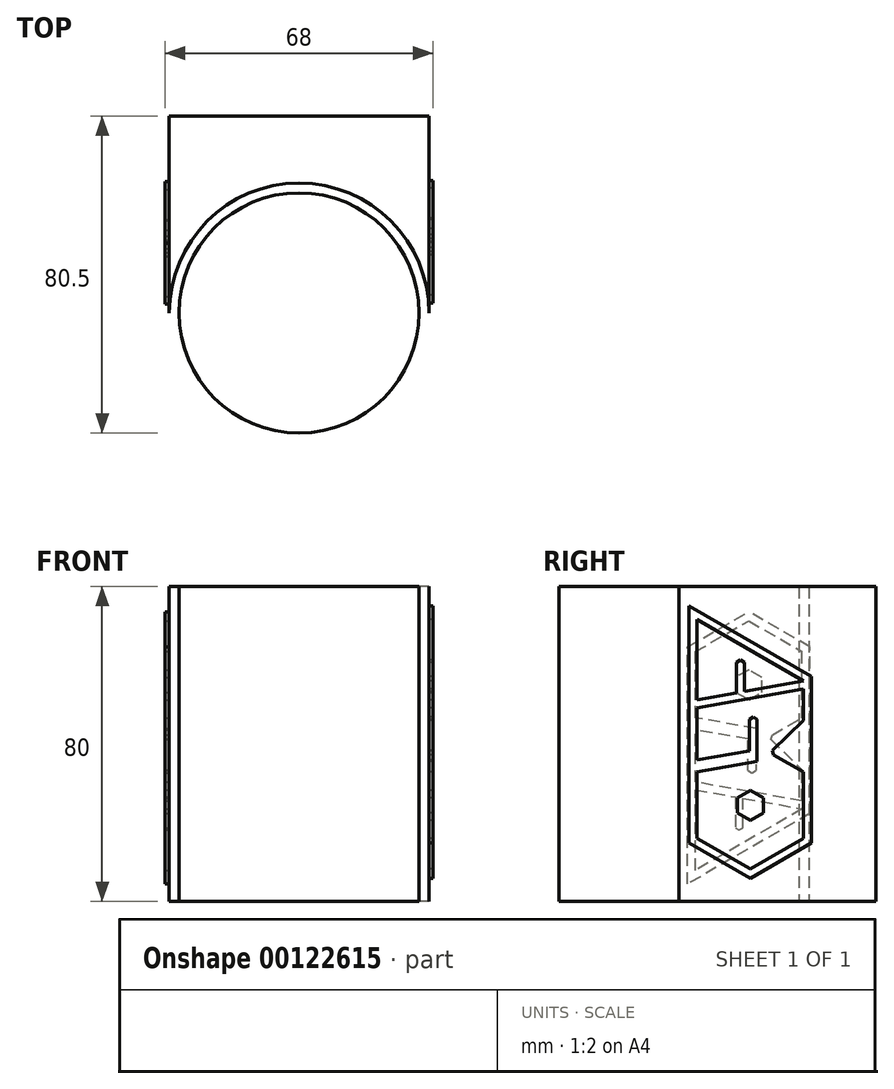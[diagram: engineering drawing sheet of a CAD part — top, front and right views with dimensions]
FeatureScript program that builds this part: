
annotation { "Feature Type Name" : "Feature", "Feature Type Description" : "" }
export const myFeature = defineFeature(function(context is Context, id is Id, definition is map)
    precondition{}
    {
        {
            var Q0;
            Q0=qCreatedBy(makeId("Top.planeOp"),FACE);
            var sketch = newSketch(context, id + "F5", { "sketchPlane" : qUnion([Q0])});
            skLineSegment(sketch, "E0", {"start": v(-33, 0) * mm, "end": v(-33, 50) * mm});
            skLineSegment(sketch, "E1.MirrorCS", {"start": v(-33, 50) * mm, "end": v(-79, 50) * mm});
            skLineSegment(sketch, "E2.MirrorCS", {"start": v(-79, 35) * mm, "end": v(-79, 50) * mm});
            skLineSegment(sketch, "E3.MirrorCS", {"start": v(-79, 35) * mm, "end": v(-99, 35) * mm});
            skLineSegment(sketch, "E4.MirrorCS", {"start": v(-99, 35) * mm, "end": v(-99, 0) * mm});
            skCircle(sketch, "E5.MirrorC", {"center": v(-66, 0) * mm, "radius": 33 * mm});
            skCircle(sketch, "E6.MirrorC", {"center": v(-66, 0) * mm, "radius": 30.5 * mm});
            skLineSegment(sketch, "E7", {"start": v(-99, 35) * mm, "end": v(-99, 50) * mm});
            skLineSegment(sketch, "E8", {"start": v(-99, 50) * mm, "end": v(-79, 50) * mm});
            skSolve(sketch);
        }
        {
            var Q0;
            {var subQ0=sQuery(id+"F5.wireOp",EDGE,"E0");Q0=makeQuery(id+"F5.imprint","IMPRINT",FACE,{"disambiguationData":[TD([[makeQuery(id+"F5.imprint","IMPRINT",EDGE,{"derivedFrom":subQ0}),1.0]])]});}
            var Q1;
            Q1=makeQuery(id+"F5.imprint","IMPRINT",FACE,{"disambiguationData":[TD([[makeQuery(id+"F5.imprint","IMPRINT",EDGE,{"derivedFrom":sQuery(id+"F5.wireOp",EDGE,"E6.MirrorC")}),1.0]])]});
            var Q2;
            Q2=makeQuery(id+"F5.imprint","IMPRINT",FACE,{"disambiguationData":[TD([[makeQuery(id+"F5.imprint","IMPRINT",EDGE,{"derivedFrom":sQuery(id+"F5.wireOp",EDGE,"E2.MirrorCS")}),1.0]])]});
            extrude(context, id + "F0", {"entities" : qUnion([Q0, Q1, Q2]), "depth" : 80 * mm});
        }
        {
            var Q0;
            Q0=makeQuery(id+"F0.opExtrude","SWEPT_FACE",FACE,{"disambiguationData":[OSD([sQuery(id+"F5.wireOp",EDGE,"E0")])]});
            var sketch = newSketch(context, id + "F1", { "sketchPlane" : qUnion([Q0])});
            skLineSegment(sketch, "E9", {"start": v(4.56, 71.6) * mm, "end": v(4.56, 51.17) * mm});
            skLineSegment(sketch, "E10", {"start": v(4.56, 51.17) * mm, "end": v(31.66, 55.94) * mm});
            skLineSegment(sketch, "E11", {"start": v(31.66, 55.94) * mm, "end": v(4.56, 71.6) * mm});
            skLineSegment(sketch, "E12", {"start": v(14.65, 52.94) * mm, "end": v(14.65, 60.74) * mm});
            skLineSegment(sketch, "E13", {"start": v(4.56, 51.17) * mm, "end": v(4.56, 16.02) * mm});
            skLineSegment(sketch, "E14", {"start": v(31.66, 55.94) * mm, "end": v(31.66, 16.02) * mm});
            skLineSegment(sketch, "E15", {"start": v(4.56, 16.02) * mm, "end": v(18.11, 8.2) * mm});
            skLineSegment(sketch, "E16", {"start": v(18.11, 8.2) * mm, "end": v(31.66, 16.02) * mm});
            skPoint(sketch, "E17.endSnap0", {"position": v(18.11, 53.55) * mm});
            skLineSegment(sketch, "E18.0", {"start": v(33.66, 57.1) * mm, "end": v(33.66, 15.6) * mm});
            skLineSegment(sketch, "E18.1", {"start": v(2.56, 75.05) * mm, "end": v(2.56, 51.65) * mm});
            skLineSegment(sketch, "E18.2", {"start": v(2.56, 51.65) * mm, "end": v(2.56, 14.87) * mm});
            skLineSegment(sketch, "E18.3", {"start": v(33.66, 57.1) * mm, "end": v(2.56, 75.05) * mm});
            skLineSegment(sketch, "E18.4", {"start": v(2.56, 14.87) * mm, "end": v(18.11, 5.89) * mm});
            skLineSegment(sketch, "E19", {"start": v(16.65, 60.74) * mm, "end": v(16.65, 53.3) * mm});
            skLineSegment(sketch, "E20", {"start": v(31.66, 53.94) * mm, "end": v(4.56, 49.17) * mm});
            skLineSegment(sketch, "E21", {"start": v(31.66, 55.94) * mm, "end": v(31.66, 53.94) * mm});
            skLineSegment(sketch, "E22", {"start": v(4.56, 36.26) * mm, "end": v(4.56, 38.26) * mm});
            skLineSegment(sketch, "E23", {"start": v(17.87, 46.23) * mm, "end": v(17.87, 38.26) * mm});
            skLineSegment(sketch, "E24", {"start": v(19.87, 35.53) * mm, "end": v(19.87, 46.23) * mm});
            skLineSegment(sketch, "E25", {"start": v(23.78, 38.34) * mm, "end": v(31.66, 46.02) * mm});
            skLineSegment(sketch, "E26", {"start": v(14.65, 60.74) * mm, "end": v(15.65, 61.32) * mm});
            skLineSegment(sketch, "E27", {"start": v(15.65, 61.32) * mm, "end": v(16.65, 60.74) * mm});
            skLineSegment(sketch, "E28", {"start": v(17.87, 46.23) * mm, "end": v(18.87, 46.8) * mm});
            skLineSegment(sketch, "E29", {"start": v(18.87, 46.8) * mm, "end": v(19.87, 46.23) * mm});
            skLineSegment(sketch, "E30", {"start": v(25.18, 36.9) * mm, "end": v(31.66, 43.27) * mm});
            skLineSegment(sketch, "E31", {"start": v(23.78, 38.34) * mm, "end": v(24.07, 37.21) * mm});
            skLineSegment(sketch, "E32", {"start": v(24.07, 37.21) * mm, "end": v(25.18, 36.9) * mm});
            skLineSegment(sketch, "E33", {"start": v(17.87, 38.26) * mm, "end": v(4.56, 35.91) * mm});
            skLineSegment(sketch, "E34", {"start": v(19.87, 35.53) * mm, "end": v(4.56, 32.83) * mm});
            skLineSegment(sketch, "E35", {"start": v(24.07, 37.21) * mm, "end": v(31.66, 32.83) * mm});
            skLineSegment(sketch, "E36", {"start": v(31.66, 32.83) * mm, "end": v(31.66, 16.02) * mm});
            skLineSegment(sketch, "E37", {"start": v(4.56, 32.83) * mm, "end": v(4.56, 16.02) * mm});
            skPoint(sketch, "E38", {"position": v(31.66, 24.42) * mm});
            skPoint(sketch, "E39", {"position": v(18.11, 24.42) * mm});
            skCircle(sketch, "E40.cCircle", {"center": v(18.11, 24.42) * mm, "radius": 3.3 * mm, "construction": true});
            skLineSegment(sketch, "E40.0", {"start": v(21.41, 26.33) * mm, "end": v(21.41, 22.52) * mm});
            skLineSegment(sketch, "E40.1", {"start": v(21.41, 22.52) * mm, "end": v(18.11, 20.61) * mm});
            skLineSegment(sketch, "E40.2", {"start": v(18.11, 20.61) * mm, "end": v(14.81, 22.52) * mm});
            skLineSegment(sketch, "E40.3", {"start": v(14.81, 22.52) * mm, "end": v(14.81, 26.33) * mm});
            skLineSegment(sketch, "E40.4", {"start": v(14.81, 26.33) * mm, "end": v(18.11, 28.24) * mm});
            skLineSegment(sketch, "E40.5", {"start": v(18.11, 28.24) * mm, "end": v(21.41, 26.33) * mm});
            skPoint(sketch, "E40.0.midPoint", {"position": v(21.41, 24.42) * mm});
            skLineSegment(sketch, "E41.0", {"start": v(19.11, 6.46) * mm, "end": v(33.66, 14.87) * mm});
            skLineSegment(sketch, "E41.1", {"start": v(33.66, 32.83) * mm, "end": v(33.66, 14.87) * mm});
            skLineSegment(sketch, "E42", {"start": v(19.11, 6.46) * mm, "end": v(18.11, 5.89) * mm});
            skSolve(sketch);
        }
        {
            var Q0;
            {var subQ14=sQuery(id+"F1.wireOp",EDGE,"E9");Q0=makeQuery(id+"F1.imprint","IMPRINT",FACE,{"disambiguationData":[TD([[makeQuery(id+"F1.imprint","IMPRINT",EDGE,{"derivedFrom":subQ14}),-1.0]])]});}
            var Q1;
            {var subQ3=sQuery(id+"F1.wireOp",EDGE,"E20");Q1=makeQuery(id+"F1.imprint","IMPRINT",FACE,{"disambiguationData":[TD([[makeQuery(id+"F1.imprint","IMPRINT",EDGE,{"derivedFrom":subQ3}),-1.0]])]});}
            var Q2;
            {var subQ0=sQuery(id+"F1.wireOp",EDGE,"E12");Q2=makeQuery(id+"F1.imprint","IMPRINT",FACE,{"disambiguationData":[TD([[makeQuery(id+"F1.imprint","IMPRINT",EDGE,{"derivedFrom":subQ0}),-1.0]])]});}
            var Q3;
            Q3=makeQuery(id+"F1.imprint","IMPRINT",FACE,{"disambiguationData":[TD([[makeQuery(id+"F1.imprint","IMPRINT",EDGE,{"derivedFrom":sQuery(id+"F1.wireOp",EDGE,"E23")}),1.0]])]});
            var Q4;
            {var subQ1=sQuery(id+"F1.wireOp",EDGE,"E25");Q4=makeQuery(id+"F1.imprint","IMPRINT",FACE,{"disambiguationData":[TD([[makeQuery(id+"F1.imprint","IMPRINT",EDGE,{"derivedFrom":subQ1}),-1.0]])]});}
            var Q5;
            {var subQ2=sQuery(id+"F1.wireOp",EDGE,"E30");Q5=makeQuery(id+"F1.imprint","IMPRINT",FACE,{"disambiguationData":[TD([[makeQuery(id+"F1.imprint","IMPRINT",EDGE,{"derivedFrom":subQ2}),-1.0]])]});}
            var Q6;
            Q6=makeQuery(id+"F1.imprint","IMPRINT",FACE,{"disambiguationData":[TD([[makeQuery(id+"F1.imprint","IMPRINT",EDGE,{"derivedFrom":sQuery(id+"F1.wireOp",EDGE,"E40.0")}),-1.0]])]});
            extrude(context, id + "F2", {"entities" : qUnion([Q0, Q1, Q2, Q3, Q4, Q5, Q6]), "operationType" : NewBodyOperationType.ADD, "depth" : 1 * mm});
        }
        {
            var Q0;
            Q0=makeQuery(id+"F0.opExtrude","SWEPT_FACE",FACE,{"disambiguationData":[OSD([sQuery(id+"F5.wireOp",EDGE,"E4.MirrorCS")])]});
            var sketch = newSketch(context, id + "F3", { "sketchPlane" : qUnion([Q0])});
            skLineSegment(sketch, "E43", {"start": v(-4.22, 7.88) * mm, "end": v(-4.22, 28.3) * mm});
            skLineSegment(sketch, "E44", {"start": v(-4.22, 28.3) * mm, "end": v(-31.32, 23.52) * mm});
            skLineSegment(sketch, "E45", {"start": v(-31.32, 23.52) * mm, "end": v(-4.22, 7.88) * mm});
            skLineSegment(sketch, "E46", {"start": v(-14.3, 26.52) * mm, "end": v(-14.3, 18.72) * mm});
            skLineSegment(sketch, "E47", {"start": v(-4.22, 28.3) * mm, "end": v(-4.22, 63.45) * mm});
            skLineSegment(sketch, "E48", {"start": v(-31.32, 23.52) * mm, "end": v(-31.32, 63.45) * mm});
            skLineSegment(sketch, "E49", {"start": v(-4.22, 63.45) * mm, "end": v(-17.77, 71.27) * mm});
            skLineSegment(sketch, "E50", {"start": v(-17.77, 71.27) * mm, "end": v(-31.32, 63.45) * mm});
            skPoint(sketch, "E51.endSnap0", {"position": v(-17.77, 25.91) * mm});
            skLineSegment(sketch, "E52.0", {"start": v(-33.32, 22.37) * mm, "end": v(-33.32, 63.87) * mm});
            skLineSegment(sketch, "E52.1", {"start": v(-2.22, 4.41) * mm, "end": v(-2.22, 27.82) * mm});
            skLineSegment(sketch, "E52.2", {"start": v(-2.22, 27.82) * mm, "end": v(-2.22, 64.6) * mm});
            skLineSegment(sketch, "E52.3", {"start": v(-33.32, 22.37) * mm, "end": v(-2.22, 4.41) * mm});
            skLineSegment(sketch, "E52.4", {"start": v(-2.22, 64.6) * mm, "end": v(-17.77, 73.58) * mm});
            skLineSegment(sketch, "E53", {"start": v(-16.3, 18.72) * mm, "end": v(-16.3, 26.17) * mm});
            skLineSegment(sketch, "E54", {"start": v(-31.32, 25.52) * mm, "end": v(-4.22, 30.3) * mm});
            skLineSegment(sketch, "E55", {"start": v(-31.32, 23.52) * mm, "end": v(-31.32, 25.52) * mm});
            skLineSegment(sketch, "E56", {"start": v(-4.22, 43.2) * mm, "end": v(-4.22, 41.2) * mm});
            skLineSegment(sketch, "E57", {"start": v(-17.53, 33.24) * mm, "end": v(-17.53, 41.2) * mm});
            skLineSegment(sketch, "E58", {"start": v(-19.53, 43.94) * mm, "end": v(-19.53, 33.24) * mm});
            skLineSegment(sketch, "E59", {"start": v(-23.44, 41.13) * mm, "end": v(-31.32, 33.45) * mm});
            skLineSegment(sketch, "E60", {"start": v(-14.3, 18.72) * mm, "end": v(-15.3, 18.15) * mm});
            skLineSegment(sketch, "E61", {"start": v(-15.3, 18.15) * mm, "end": v(-16.3, 18.72) * mm});
            skLineSegment(sketch, "E62", {"start": v(-17.53, 33.24) * mm, "end": v(-18.53, 32.67) * mm});
            skLineSegment(sketch, "E63", {"start": v(-18.53, 32.67) * mm, "end": v(-19.53, 33.24) * mm});
            skLineSegment(sketch, "E64", {"start": v(-24.83, 42.56) * mm, "end": v(-31.32, 36.2) * mm});
            skLineSegment(sketch, "E65", {"start": v(-23.44, 41.13) * mm, "end": v(-23.72, 42.25) * mm});
            skLineSegment(sketch, "E66", {"start": v(-23.72, 42.25) * mm, "end": v(-24.83, 42.56) * mm});
            skLineSegment(sketch, "E67", {"start": v(-17.53, 41.2) * mm, "end": v(-4.22, 43.56) * mm});
            skLineSegment(sketch, "E68", {"start": v(-19.53, 43.94) * mm, "end": v(-4.22, 46.64) * mm});
            skLineSegment(sketch, "E69", {"start": v(-23.72, 42.25) * mm, "end": v(-31.32, 46.64) * mm});
            skLineSegment(sketch, "E70", {"start": v(-31.32, 46.64) * mm, "end": v(-31.32, 63.45) * mm});
            skLineSegment(sketch, "E71", {"start": v(-4.22, 46.64) * mm, "end": v(-4.22, 63.45) * mm});
            skPoint(sketch, "E72", {"position": v(-31.32, 55.04) * mm});
            skPoint(sketch, "E73", {"position": v(-17.77, 55.04) * mm});
            skCircle(sketch, "E74.cCircle", {"center": v(-17.77, 55.04) * mm, "radius": 3.3 * mm, "construction": true});
            skLineSegment(sketch, "E74.0", {"start": v(-21.07, 53.14) * mm, "end": v(-21.07, 56.95) * mm});
            skLineSegment(sketch, "E74.1", {"start": v(-21.07, 56.95) * mm, "end": v(-17.77, 58.85) * mm});
            skLineSegment(sketch, "E74.2", {"start": v(-17.77, 58.85) * mm, "end": v(-14.47, 56.95) * mm});
            skLineSegment(sketch, "E74.3", {"start": v(-14.47, 56.95) * mm, "end": v(-14.47, 53.14) * mm});
            skLineSegment(sketch, "E74.4", {"start": v(-14.47, 53.14) * mm, "end": v(-17.77, 51.23) * mm});
            skLineSegment(sketch, "E74.5", {"start": v(-17.77, 51.23) * mm, "end": v(-21.07, 53.14) * mm});
            skPoint(sketch, "E74.0.midPoint", {"position": v(-21.07, 55.04) * mm});
            skLineSegment(sketch, "E75.0", {"start": v(-18.77, 73) * mm, "end": v(-33.32, 64.6) * mm});
            skLineSegment(sketch, "E75.1", {"start": v(-33.32, 46.64) * mm, "end": v(-33.32, 64.6) * mm});
            skLineSegment(sketch, "E76", {"start": v(-18.77, 73) * mm, "end": v(-17.77, 73.58) * mm});
            skSolve(sketch);
        }
        {
            var Q0;
            {var subQ9=sQuery(id+"F3.wireOp",EDGE,"E43");Q0=makeQuery(id+"F3.imprint","IMPRINT",FACE,{"disambiguationData":[TD([[makeQuery(id+"F3.imprint","IMPRINT",EDGE,{"derivedFrom":subQ9}),-1.0]])]});}
            var Q1;
            Q1=makeQuery(id+"F3.imprint","IMPRINT",FACE,{"disambiguationData":[TD([[makeQuery(id+"F3.imprint","IMPRINT",EDGE,{"derivedFrom":sQuery(id+"F3.wireOp",EDGE,"E57")}),1.0]])]});
            var Q2;
            {var subQ1=sQuery(id+"F3.wireOp",EDGE,"E59");Q2=makeQuery(id+"F3.imprint","IMPRINT",FACE,{"disambiguationData":[TD([[makeQuery(id+"F3.imprint","IMPRINT",EDGE,{"derivedFrom":subQ1}),-1.0]])]});}
            var Q3;
            {var subQ2=sQuery(id+"F3.wireOp",EDGE,"E64");Q3=makeQuery(id+"F3.imprint","IMPRINT",FACE,{"disambiguationData":[TD([[makeQuery(id+"F3.imprint","IMPRINT",EDGE,{"derivedFrom":subQ2}),-1.0]])]});}
            var Q4;
            Q4=makeQuery(id+"F3.imprint","IMPRINT",FACE,{"disambiguationData":[TD([[makeQuery(id+"F3.imprint","IMPRINT",EDGE,{"derivedFrom":sQuery(id+"F3.wireOp",EDGE,"E74.0")}),-1.0]])]});
            var Q5;
            {var subQ5=sQuery(id+"F3.wireOp",EDGE,"E54");Q5=makeQuery(id+"F3.imprint","IMPRINT",FACE,{"disambiguationData":[TD([[makeQuery(id+"F3.imprint","IMPRINT",EDGE,{"derivedFrom":subQ5}),-1.0]])]});}
            var Q6;
            {var subQ1=sQuery(id+"F3.wireOp",EDGE,"E46");Q6=makeQuery(id+"F3.imprint","IMPRINT",FACE,{"disambiguationData":[TD([[makeQuery(id+"F3.imprint","IMPRINT",EDGE,{"derivedFrom":subQ1}),-1.0]])]});}
            extrude(context, id + "F4", {"entities" : qUnion([Q0, Q1, Q2, Q3, Q4, Q5, Q6]), "operationType" : NewBodyOperationType.ADD, "depth" : 1 * mm});
        }
    });
